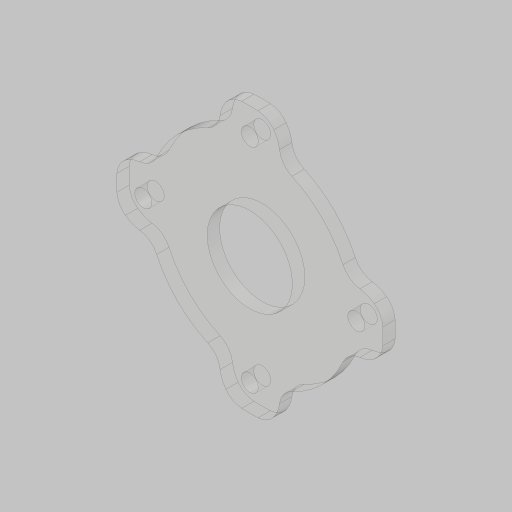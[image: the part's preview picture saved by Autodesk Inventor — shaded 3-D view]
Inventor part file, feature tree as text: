
AUTODESK INVENTOR PART (.ipt)
format: ipt  version: 2023.5 (Build 275446000, 446)  size: 194,048 bytes
history: native  units: in
note: dims shown in document units (in); Inventor stores cm internally (conversion verified against a paired STEP export)
features: extrude x3, sketch x2, hole x1, mirror x1, fillet x1, projected_geometry x1
ambient origin geometry x8: Origin, YZ Plane, XZ Plane, XY Plane, X Axis, Y Axis, Z Axis, Center Point
bodies: Solid1 (feature_tree)
feature tree (9):
  sketch  "Sketch1"  dims[d0=1.875in d1=0.625in]
  extrude  "Extrusion1"  Depth=0.625in
  extrude  "Extrusion2"  Depth=0.145in TaperAngle=0.0deg
  hole  "Hole1"  [1 undecoded]
  extrude  "Extrusion3"  Depth=0.25in TaperAngle=0.0deg
  mirror  "Mirror1"
  fillet  "Fillet1"  Radius=0.25in
  sketch  "Sketch2"  dims[d2=2.5in d3=0.145in d4=0.0in d5=1.0in d6=0.25in d7=0.0in d8=0.201in d9=0.38in d10=0.385in d11=0.25in d12=0.5635in d13=1.0in d14=0.8108in d15=0.25in d16=0.25in d18=0.25in d19=0.25in d20=45.0deg d21=0.25in d22=45.0deg d23=0.25in d24=0.0in d25=0.25in d26=0.25in d27=0.25in]
  projected_geometry  "Project Cut Edges1"
note: 1 required parameter value undecoded (feature->parameter linkage not recoverable at this tier; creation-order binding heuristic only, values carry confidence <= 0.55)
